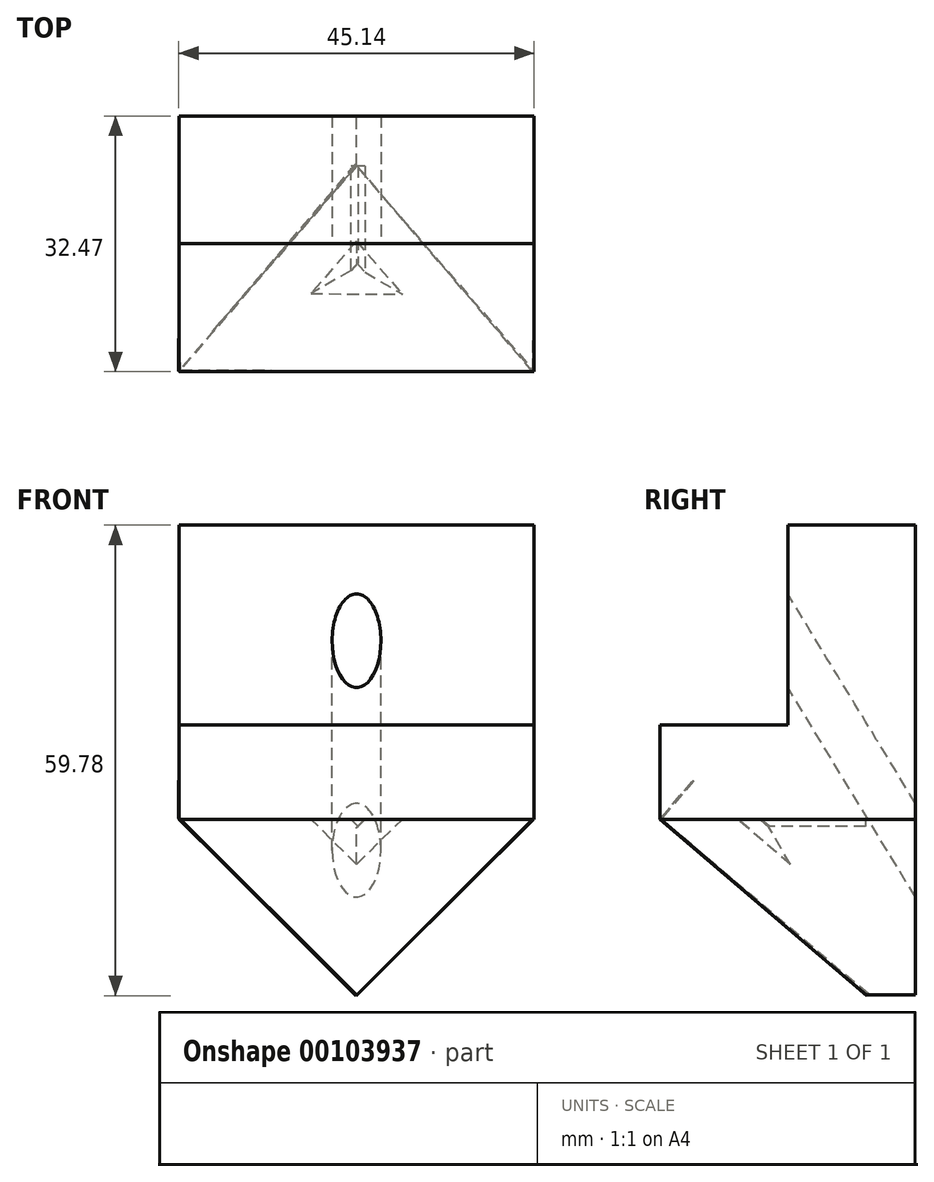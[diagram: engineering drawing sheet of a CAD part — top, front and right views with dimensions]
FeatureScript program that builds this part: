
annotation { "Feature Type Name" : "Feature", "Feature Type Description" : "" }
export const myFeature = defineFeature(function(context is Context, id is Id, definition is map)
    precondition{}
    {
        {
            var Q0;
            Q0=qCreatedBy(makeId("Front.planeOp"),FACE);
            var sketch = newSketch(context, id + "F0", { "sketchPlane" : qUnion([Q0])});
            skLineSegment(sketch, "E0.bottom", {"start": v(22.54, 5.98) * mm, "end": v(-22.54, 5.98) * mm});
            skLineSegment(sketch, "E0.top", {"start": v(22.54, -5.98) * mm, "end": v(-22.54, -5.98) * mm});
            skLineSegment(sketch, "E0.left", {"start": v(22.54, 5.98) * mm, "end": v(22.54, -5.98) * mm});
            skLineSegment(sketch, "E0.right", {"start": v(-22.54, 5.98) * mm, "end": v(-22.54, -5.98) * mm});
            skPoint(sketch, "E0.middle", {"position": v(0, 0) * mm});
            skSolve(sketch);
        }
        {
            var Q0;
            Q0 = qSketchRegion(id + "F0", true);
            extrude(context, id + "F1", {"entities" : qUnion([Q0]), "depth" : 32.47 * mm});
        }
        {
            var Q0;
            Q0=makeQuery(id+"F1.opExtrude","CAP_FACE",FACE,{"disambiguationData":[OSD([sQuery(id+"F0.wireOp",EDGE,"E0.bottom"),sQuery(id+"F0.wireOp",EDGE,"E0.top"),sQuery(id+"F0.wireOp",EDGE,"E0.left"),sQuery(id+"F0.wireOp",EDGE,"E0.right")])],"isStart":true});
            var sketch = newSketch(context, id + "F2", { "sketchPlane" : qUnion([Q0])});
            skLineSegment(sketch, "E1", {"start": v(0, -5.98) * mm, "end": v(0, -28.27) * mm, "construction": true});
            skPoint(sketch, "E1.endSnap0", {"position": v(0, -5.98) * mm});
            skLineSegment(sketch, "E2", {"start": v(0, -28.27) * mm, "end": v(22.54, -5.98) * mm});
            skLineSegment(sketch, "E3", {"start": v(-22.54, -5.98) * mm, "end": v(0, -28.27) * mm});
            skLineSegment(sketch, "E4", {"start": v(-22.54, -5.98) * mm, "end": v(22.54, -5.98) * mm});
            skSolve(sketch);
        }
        {
            var Q0;
            Q0 = qSketchRegion(id + "F2", true);
            extrude(context, id + "F3", {"entities" : qUnion([Q0]), "operationType" : NewBodyOperationType.ADD, "oppositeDirection" : true, "depth" : 6.35 * mm});
        }
        {
            var Q0;
            Q0=makeQuery(id+"F1.opExtrude","SWEPT_FACE",FACE,{"disambiguationData":[OSD([sQuery(id+"F0.wireOp",EDGE,"E0.bottom")])]});
            var sketch = newSketch(context, id + "F4", { "sketchPlane" : qUnion([Q0])});
            skLineSegment(sketch, "E5.bottom", {"start": v(-22.54, 0) * mm, "end": v(22.54, 0) * mm});
            skLineSegment(sketch, "E5.top", {"start": v(-22.54, -16.24) * mm, "end": v(22.54, -16.24) * mm});
            skLineSegment(sketch, "E5.left", {"start": v(-22.54, 0) * mm, "end": v(-22.54, -16.24) * mm});
            skLineSegment(sketch, "E5.right", {"start": v(22.54, 0) * mm, "end": v(22.54, -16.24) * mm});
            skSolve(sketch);
        }
        {
            var Q0;
            Q0 = qSketchRegion(id + "F4", true);
            extrude(context, id + "F5", {"entities" : qUnion([Q0]), "operationType" : NewBodyOperationType.ADD, "depth" : 25.4 * mm});
        }
        {
            var Q0;
            Q0=makeQuery(id+"F3.opExtrude","SWEPT_FACE",FACE,{"disambiguationData":[OSD([sQuery(id+"F2.wireOp",EDGE,"E2")])]});
            var sketch = newSketch(context, id + "F6", { "sketchPlane" : qUnion([Q0])});
            skLineSegment(sketch, "E6", {"start": v(19.87, 6.35) * mm, "end": v(-11.7, 32.25) * mm});
            skLineSegment(sketch, "E7", {"start": v(-11.7, 32.25) * mm, "end": v(-11.82, 6.35) * mm});
            skLineSegment(sketch, "E8", {"start": v(-11.82, 6.35) * mm, "end": v(19.87, 6.35) * mm});
            skSolve(sketch);
        }
        {
            var Q0;
            Q0 = qSketchRegion(id + "F6", true);
            extrude(context, id + "F7", {"entities" : qUnion([Q0]), "operationType" : NewBodyOperationType.ADD, "oppositeDirection" : true, "depth" : 15.33 * mm});
        }
        {
            var Q0;
            Q0=makeQuery(id+"F3.opExtrude","SWEPT_FACE",FACE,{"disambiguationData":[OSD([sQuery(id+"F2.wireOp",EDGE,"E3")])]});
            var sketch = newSketch(context, id + "F8", { "sketchPlane" : qUnion([Q0])});
            skLineSegment(sketch, "E9", {"start": v(-19.87, 6.35) * mm, "end": v(11.82, 6.35) * mm});
            skLineSegment(sketch, "E10", {"start": v(-19.87, 6.35) * mm, "end": v(11.74, 32.34) * mm});
            skLineSegment(sketch, "E11", {"start": v(11.74, 32.34) * mm, "end": v(11.82, 6.35) * mm});
            skSolve(sketch);
        }
        {
            var Q0;
            Q0 = qSketchRegion(id + "F8", true);
            extrude(context, id + "F9", {"entities" : qUnion([Q0]), "operationType" : NewBodyOperationType.ADD, "oppositeDirection" : true, "depth" : 15.1 * mm});
        }
        {
            var Q0;
            {var subQ0=sQuery(id+"F2.wireOp",EDGE,"E3");var subQ1=sQuery(id+"F2.wireOp",EDGE,"E2");Q0=makeQuery(id+"F9.boolean.opBoolean","MERGE",VERTEX,{"derivedFrom":[makeQuery(id+"F7.boolean.opBoolean","MERGE",VERTEX,{"derivedFrom":[makeQuery(id+"F3.opExtrude","CAP_VERTEX",VERTEX,{"disambiguationData":[OSD([subQ1,subQ0])],"isStart":false}),makeQuery(id+"F7.opExtrude","CAP_VERTEX",VERTEX,{"disambiguationData":[OSD([subQ1,subQ0,sQuery(id+"F6.wireOp",EDGE,"E6"),sQuery(id+"F6.wireOp",EDGE,"E8")])],"isStart":true})]}),makeQuery(id+"F9.opExtrude","CAP_VERTEX",VERTEX,{"disambiguationData":[OSD([subQ1,subQ0,sQuery(id+"F8.wireOp",EDGE,"E9"),sQuery(id+"F8.wireOp",EDGE,"E10")])],"isStart":true})]});}
            var Q1;
            Q1=makeQuery(id+"F1.opExtrude","CAP_VERTEX",VERTEX,{"disambiguationData":[OSD([sQuery(id+"F0.wireOp",EDGE,"E0.top"),sQuery(id+"F0.wireOp",EDGE,"E0.left")])],"isStart":false});
            var Q2;
            Q2=makeQuery(id+"F7.boolean.opBoolean","INTERSECT",VERTEX,{"derivedFrom":[makeQuery(id+"F1.opExtrude","SWEPT_FACE",FACE,{"disambiguationData":[OSD([sQuery(id+"F0.wireOp",EDGE,"E0.top")])]}),makeQuery(id+"F7.opExtrude","SWEPT_FACE",FACE,{"disambiguationData":[OSD([sQuery(id+"F6.wireOp",EDGE,"E6")])]}),makeQuery(id+"F7.opExtrude","SWEPT_FACE",FACE,{"disambiguationData":[OSD([sQuery(id+"F6.wireOp",EDGE,"E7")])]})]});
            cPlane(context, id + "F10", {"entities" : qUnion([Q0, Q1, Q2]), "cplaneType" : CPlaneType.THREE_POINT, "offset" : 152.4 * mm, "width" : 152.4 * mm, "height" : 152.4 * mm});
        }
        {
            var Q0;
            Q0=qCreatedBy(id+"F10.planeOp",FACE);
            var sketch = newSketch(context, id + "F11", { "sketchPlane" : qUnion([Q0])});
            skLineSegment(sketch, "E12", {"start": v(0, 13.77) * mm, "end": v(-22.52, -20.76) * mm});
            skLineSegment(sketch, "E13", {"start": v(-22.52, -20.76) * mm, "end": v(22.45, -20.76) * mm});
            skLineSegment(sketch, "E14", {"start": v(22.45, -20.76) * mm, "end": v(0, 13.77) * mm});
            skSolve(sketch);
        }
        {
            var Q0;
            Q0 = qSketchRegion(id + "F11", true);
            extrude(context, id + "F12", {"entities" : qUnion([Q0]), "operationType" : NewBodyOperationType.ADD, "depth" : 6.35 * mm});
        }
        {
            var Q0;
            Q0=makeQuery(id+"F1.opExtrude","SWEPT_FACE",FACE,{"disambiguationData":[OSD([sQuery(id+"F0.wireOp",EDGE,"E0.bottom")])]});
            var sketch = newSketch(context, id + "F13", { "sketchPlane" : qUnion([Q0])});
            skLineSegment(sketch, "E15", {"start": v(22.54, -32.47) * mm, "end": v(22.54, -57.87) * mm});
            skLineSegment(sketch, "E16", {"start": v(-22.54, -32.47) * mm, "end": v(-22.54, -57.87) * mm});
            skSolve(sketch);
        }
        {
            var Q0;
            Q0=sQuery(id+"F13.wireOp",VERTEX,"E16.end");
            var Q1;
            Q1=sQuery(id+"F13.wireOp",VERTEX,"E15.end");
            var Q2;
            Q2=makeQuery(id+"F5.opExtrude","CAP_VERTEX",VERTEX,{"disambiguationData":[OSD([sQuery(id+"F0.wireOp",EDGE,"E0.bottom"),sQuery(id+"F0.wireOp",EDGE,"E0.left"),sQuery(id+"F4.wireOp",EDGE,"E5.top"),sQuery(id+"F4.wireOp",EDGE,"E5.right")])],"isStart":false});
            cPlane(context, id + "F14", {"entities" : qUnion([Q0, Q1, Q2]), "cplaneType" : CPlaneType.THREE_POINT, "offset" : 152.4 * mm, "width" : 152.4 * mm, "height" : 152.4 * mm});
        }
        {
            var Q0;
            Q0=qCreatedBy(id+"F14.planeOp",FACE);
            var sketch = newSketch(context, id + "F15", { "sketchPlane" : qUnion([Q0])});
            skLineSegment(sketch, "E17", {"start": v(0, 0) * mm, "end": v(0, 5.17) * mm, "construction": true});
            skCircle(sketch, "E18", {"center": v(0, 5.17) * mm, "radius": 3.1 * mm});
            skSolve(sketch);
        }
        {
            var Q0;
            Q0 = qSketchRegion(id + "F15", true);
            extrude(context, id + "F16", {"entities" : qUnion([Q0]), "operationType" : NewBodyOperationType.REMOVE, "depth" : 50.8 * mm});
        }
    });
